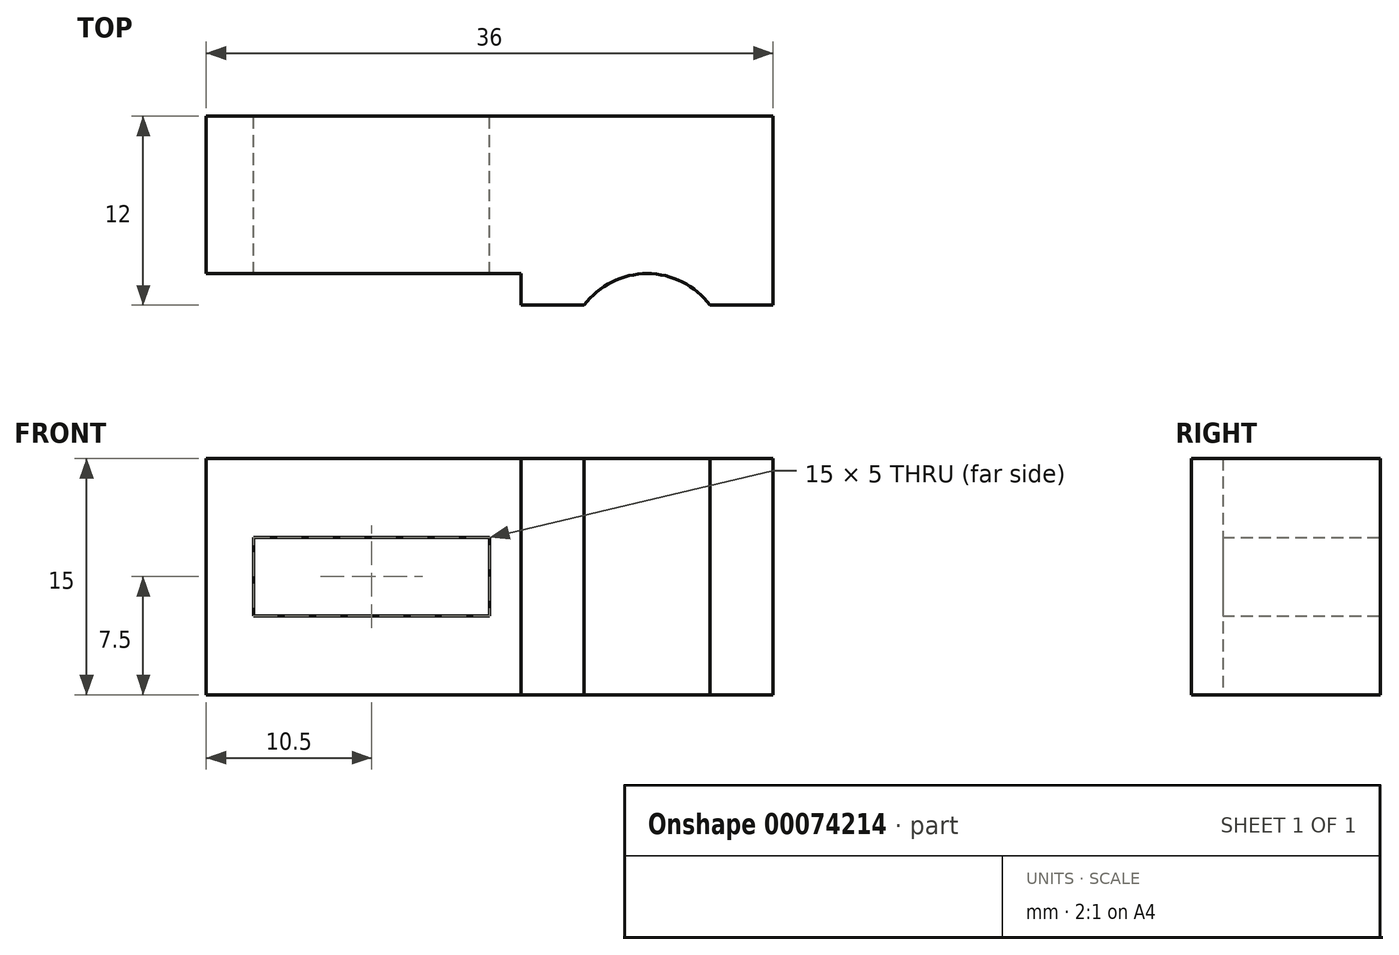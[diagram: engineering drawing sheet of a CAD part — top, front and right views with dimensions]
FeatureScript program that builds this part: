
annotation { "Feature Type Name" : "Feature", "Feature Type Description" : "" }
export const myFeature = defineFeature(function(context is Context, id is Id, definition is map)
    precondition{}
    {
        {
            var Q0;
            Q0=qCreatedBy(makeId("Top.planeOp"),FACE);
            var sketch = newSketch(context, id + "F0", { "sketchPlane" : qUnion([Q0])});
            skCircle(sketch, "E0", {"center": v(0, 0) * mm, "radius": 5 * mm});
            skLineSegment(sketch, "E1.rect.bottom", {"start": v(28, -15) * mm, "end": v(-28, -15) * mm});
            skLineSegment(sketch, "E1.rect.top", {"start": v(28, 15) * mm, "end": v(-28, 15) * mm});
            skLineSegment(sketch, "E1.rect.left", {"start": v(28, -15) * mm, "end": v(28, 15) * mm});
            skLineSegment(sketch, "E1.rect.right", {"start": v(-28, -15) * mm, "end": v(-28, 15) * mm});
            skSolve(sketch);
        }
        {
            var Q0;
            Q0=makeQuery(id+"F0.imprint","IMPRINT",FACE,{"disambiguationData":[TD([[makeQuery(id+"F0.imprint","IMPRINT",EDGE,{"derivedFrom":sQuery(id+"F0.wireOp",EDGE,"E0")}),-1.0]])]});
            extrude(context, id + "F1", {"entities" : qUnion([Q0]), "depth" : 15 * mm});
        }
        {
            var Q0;
            Q0=makeQuery(id+"F1.opExtrude","SWEPT_FACE",FACE,{"disambiguationData":[OSD([sQuery(id+"F0.wireOp",EDGE,"E1.rect.bottom")])]});
            var sketch = newSketch(context, id + "F2", { "sketchPlane" : qUnion([Q0])});
            skLineSegment(sketch, "E2.bottom", {"start": v(-28, 0) * mm, "end": v(28, 0) * mm});
            skLineSegment(sketch, "E2.top", {"start": v(-28, 15) * mm, "end": v(28, 15) * mm});
            skLineSegment(sketch, "E2.left", {"start": v(-28, 0) * mm, "end": v(-28, 15) * mm});
            skLineSegment(sketch, "E2.right", {"start": v(28, 0) * mm, "end": v(28, 15) * mm});
            skSolve(sketch);
        }
        {
            var Q0;
            Q0 = qSketchRegion(id + "F2", true);
            extrude(context, id + "F3", {"entities" : qUnion([Q0]), "operationType" : NewBodyOperationType.REMOVE, "oppositeDirection" : true, "depth" : 18 * mm});
        }
        {
            var Q0;
            Q0=makeQuery(id+"F1.opExtrude","SWEPT_FACE",FACE,{"disambiguationData":[OSD([sQuery(id+"F0.wireOp",EDGE,"E1.rect.top")])]});
            var sketch = newSketch(context, id + "F4", { "sketchPlane" : qUnion([Q0])});
            skLineSegment(sketch, "E3", {"start": v(10, 10) * mm, "end": v(25, 10) * mm});
            skLineSegment(sketch, "E4", {"start": v(25, 5) * mm, "end": v(10, 5) * mm});
            skLineSegment(sketch, "E5", {"start": v(10, 5) * mm, "end": v(10, 10) * mm});
            skLineSegment(sketch, "E6", {"start": v(25, 10) * mm, "end": v(25, 5) * mm});
            skSolve(sketch);
        }
        {
            var Q0;
            Q0 = qSketchRegion(id + "F4", true);
            extrude(context, id + "F5", {"entities" : qUnion([Q0]), "operationType" : NewBodyOperationType.REMOVE, "oppositeDirection" : true, "depth" : 25 * mm});
        }
        {
            var Q0;
            Q0=makeQuery(id+"F1.opExtrude","SWEPT_FACE",FACE,{"disambiguationData":[OSD([sQuery(id+"F0.wireOp",EDGE,"E1.rect.right")])]});
            var sketch = newSketch(context, id + "F6", { "sketchPlane" : qUnion([Q0])});
            skLineSegment(sketch, "E7.bottom", {"start": v(-3, 15) * mm, "end": v(-5, 15) * mm});
            skLineSegment(sketch, "E7.top", {"start": v(-3, 0) * mm, "end": v(-5, 0) * mm});
            skLineSegment(sketch, "E7.left", {"start": v(-3, 15) * mm, "end": v(-3, 0) * mm});
            skLineSegment(sketch, "E7.right", {"start": v(-5, 15) * mm, "end": v(-5, 0) * mm});
            skSolve(sketch);
        }
        {
            var Q0;
            Q0 = qSketchRegion(id + "F6", true);
            extrude(context, id + "F7", {"entities" : qUnion([Q0]), "operationType" : NewBodyOperationType.REMOVE, "oppositeDirection" : true, "depth" : 20 * mm});
        }
        {
            var Q0;
            Q0=makeQuery(id+"F1.opExtrude","SWEPT_FACE",FACE,{"disambiguationData":[OSD([sQuery(id+"F0.wireOp",EDGE,"E1.rect.left")])]});
            var sketch = newSketch(context, id + "F8", { "sketchPlane" : qUnion([Q0])});
            skLineSegment(sketch, "E8.bottom", {"start": v(3, 15) * mm, "end": v(15, 15) * mm});
            skLineSegment(sketch, "E8.top", {"start": v(3, 0) * mm, "end": v(15, 0) * mm});
            skLineSegment(sketch, "E8.left", {"start": v(3, 15) * mm, "end": v(3, 0) * mm});
            skLineSegment(sketch, "E8.right", {"start": v(15, 15) * mm, "end": v(15, 0) * mm});
            skSolve(sketch);
        }
        {
            var Q0;
            Q0 = qSketchRegion(id + "F8", true);
            extrude(context, id + "F9", {"entities" : qUnion([Q0]), "operationType" : NewBodyOperationType.REMOVE, "oppositeDirection" : true, "depth" : 20 * mm});
        }
    });
